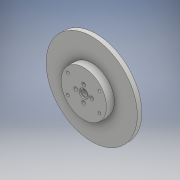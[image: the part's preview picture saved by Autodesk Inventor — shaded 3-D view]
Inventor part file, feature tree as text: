
AUTODESK INVENTOR PART (.ipt)
format: ipt  version: 2018 (Build 220112000, 112)  size: 173,056 bytes
history: native  units: mm
features: sketch x7, extrude x5, hole x2, pattern_circular x2, projected_geometry x2
ambient origin geometry x8: Origin, YZ Plane, XZ Plane, XY Plane, X Axis, Y Axis, Z Axis, Center Point
bodies: Solid1 (feature_tree)
feature tree (18):
  extrude  "Extrusion1"  Depth=7.0mm TaperAngle=0.0deg
  extrude  "Extrusion2"  Depth=4.0mm TaperAngle=0.0deg
  hole  "Hole1"  [1 undecoded]
  pattern_circular  "Circular Pattern1"  [2 undecoded]
  extrude  "Extrusion3"  Depth=6.0mm
  extrude  "Extrusion4"  Depth=4.0mm TaperAngle=0.0deg
  extrude  "Extrusion5"  Depth=6.0mm TaperAngle=360.0deg
  pattern_circular  "Circular Pattern2"  [2 undecoded]
  hole  "Hole2"  [1 undecoded]
  sketch  "Sketch1"  dims[d0=40.0mm d1=7.0mm d2=0.0mm]
  sketch  "Sketch2"  dims[d3=80.4mm d4=4.0mm d5=0.0mm]
  sketch  "Sketch3"  dims[d6=7.0mm]
  sketch  "Sketch4"  dims[d7=3.3mm d8=6.35mm d9=6.3mm d10=2.0mm d11=90.0deg d12=8.0mm d13=20.594885mm d14=40.0mm d15=360.0deg]
  sketch  "Sketch5"  dims[d17=5.5mm]
  sketch  "Sketch6"  dims[d18=10.0mm d19=0.0mm]
  projected_geometry  "Projected Loop1"
  sketch  "Sketch8"  dims[d20=8.0mm d21=1.0mm d22=0.0mm d23=5.7mm d24=4.0mm d25=0.0mm d26=40.0mm d27=360.0deg d29=17.0mm d30=28.0mm d31=7.0mm d32=7.0mm d33=2.0mm d34=2.459mm d35=6.0mm d36=9.4mm d37=2.0mm d38=90.0deg d39=8.8mm d40=20.594885mm]
  projected_geometry  "Projected Loop3"
note: 6 required parameter values undecoded (feature->parameter linkage not recoverable at this tier; creation-order binding heuristic only, values carry confidence <= 0.55)
